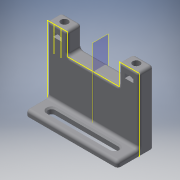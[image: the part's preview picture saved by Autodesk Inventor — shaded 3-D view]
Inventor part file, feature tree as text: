
AUTODESK INVENTOR PART (.ipt)
format: ipt  version: 2016 (Build 200138000, 138)  size: 243,200 bytes
history: native  units: mm
features: sketch x7, extrude x6, projected_geometry x5, plane x1, mirror x1, chamfer x1, fillet x1
ambient origin geometry x8: Origin, YZ Plane, XZ Plane, XY Plane, X Axis, Y Axis, Z Axis, Center Point
bodies: Solid1 (feature_tree)
feature tree (22):
  extrude  "Extrusion1"  Depth=10.0mm
  extrude  "Extrusion2"  Depth=50.0mm
  sketch  "Sketch3"  dims[d5=5.0mm d6=32.0mm]
  plane  "Work Plane1"
  extrude  "Extrusion3"  Depth=32.0mm
  sketch  "Sketch4"  dims[d7=18.0mm d8=0.0mm d9=14.0mm]
  extrude  "Extrusion4"  Depth=14.0mm
  mirror  "Mirror1"
  extrude  "Extrusion5"  Depth=15.0mm TaperAngle=0.0deg
  extrude  "Extrusion6"  Depth=3.0mm
  chamfer  "Chamfer1"  Distance=8.5mm
  fillet  "Fillet1"  Radius=4.0mm
  sketch  "Sketch1"  dims[d0=64.0mm d1=10.0mm]
  sketch  "Sketch2"  dims[d2=50.0mm d3=0.0mm d4=50.0mm]
  projected_geometry  "Projected Loop1"
  projected_geometry  "Projected Loop2"
  projected_geometry  "Projected Loop3"
  sketch  "Sketch5"  dims[d10=14.0mm d11=15.0mm d12=0.0mm]
  sketch  "Sketch6"  dims[d13=6.0mm d14=3.0mm]
  projected_geometry  "Projected Loop4"
  sketch  "Sketch7"  dims[d15=5.0mm d16=8.5mm d17=0.0mm d18=4.0mm d19=0.0mm d20=5.0mm d22=10.0mm d23=10.0mm d24=7.0mm d25=4.0mm d26=0.0mm d27=1.0mm d28=2.0mm d29=45.0deg d30=15.0mm d31=2.0mm]
  projected_geometry  "Projected Loop5"
